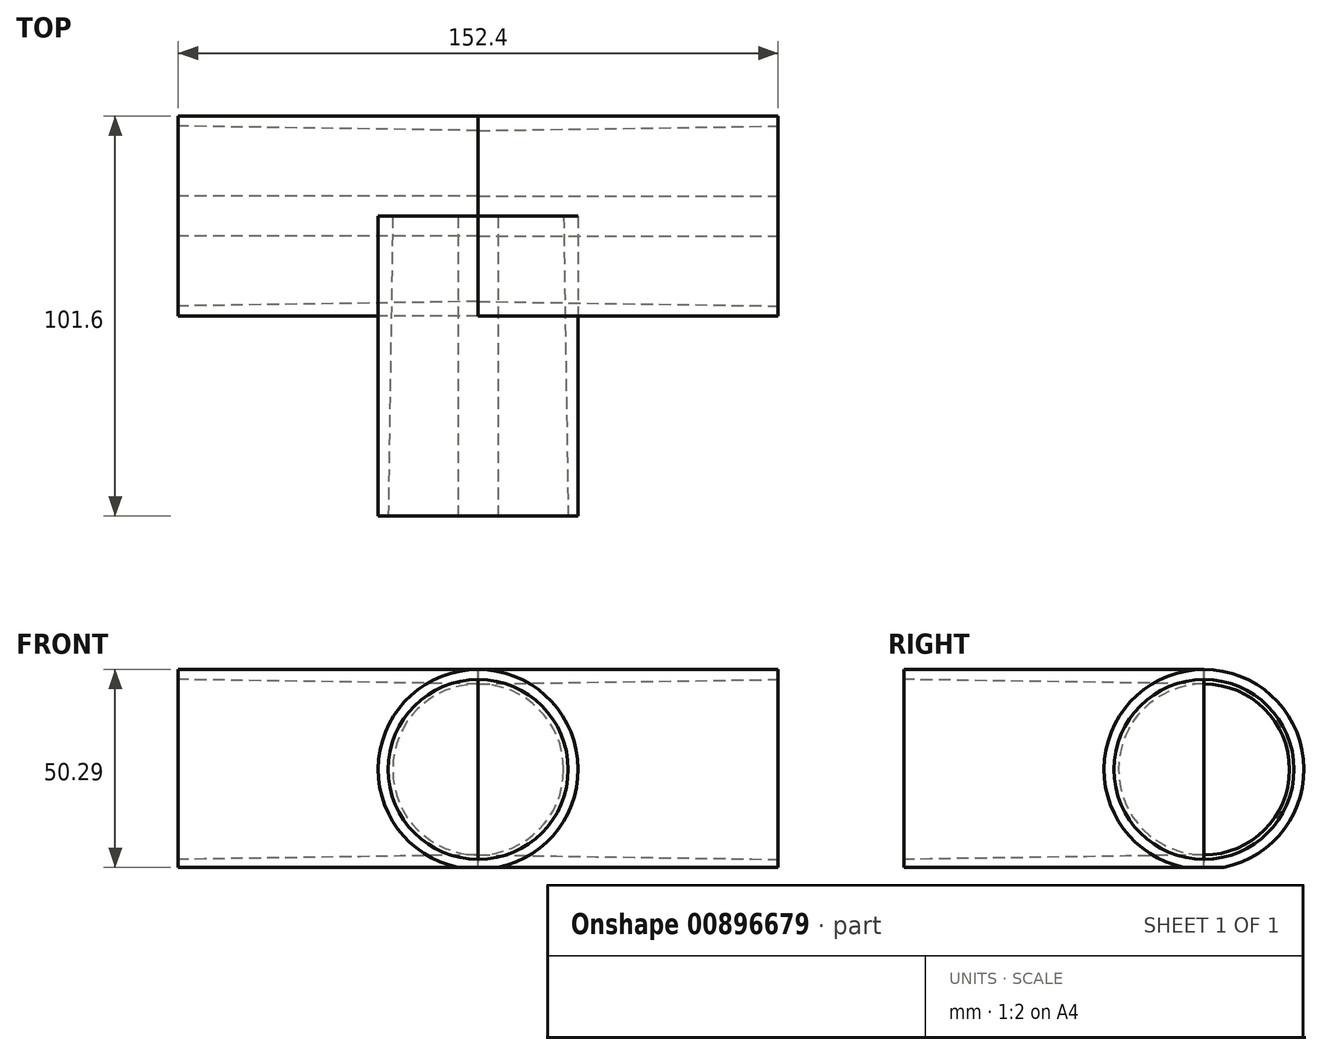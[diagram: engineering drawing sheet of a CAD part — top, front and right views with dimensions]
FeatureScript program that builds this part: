
annotation { "Feature Type Name" : "Feature", "Feature Type Description" : "" }
export const myFeature = defineFeature(function(context is Context, id is Id, definition is map)
    precondition{}
    {
        {
            var Q0;
            Q0=qCreatedBy(makeId("Front.planeOp"),FACE);
            var sketch = newSketch(context, id + "F0", { "sketchPlane" : qUnion([Q0])});
            skLineSegment(sketch, "E0", {"start": v(0, 0) * mm, "end": v(-103.9, 0) * mm, "construction": true});
            skLineSegment(sketch, "E1", {"start": v(0, 25.4) * mm, "end": v(0, 21.72) * mm});
            skLineSegment(sketch, "E2", {"start": v(0, 21.72) * mm, "end": v(76.2, 22.86) * mm});
            skLineSegment(sketch, "E3", {"start": v(76.2, 22.86) * mm, "end": v(76.2, 25.4) * mm});
            skLineSegment(sketch, "E4", {"start": v(76.2, 25.4) * mm, "end": v(0, 25.4) * mm});
            skPoint(sketch, "E5", {"position": v(50.8, 22.48) * mm});
            skSolve(sketch);
        }
        {
            var Q0;
            Q0=qSketchRegion(id+"F0",true);
            var Q1;
            Q1=sQuery(id+"F0.wireOp",EDGE,"E0");
            revolve(context, id + "F1", {"surfaceOperationType" : NewSurfaceOperationType.NEW, "entities" : qUnion([Q0]), "axis" : qUnion([Q1]), "revolveType" : RevolveType.FULL});
        }
        {
            var Q0;
            Q0=qCreatedBy(makeId("Right.planeOp"),FACE);
            cPlane(context, id + "F2", {"entities" : qUnion([Q0]), "cplaneType" : CPlaneType.OFFSET, "offset" : 0 * mm, "oppositeDirection" : true, "width" : 152.4 * mm, "height" : 152.4 * mm});
        }
        {
            var Q0;
            Q0=qCreatedBy(id+"F2.planeOp",FACE);
            var sketch = newSketch(context, id + "F3", { "sketchPlane" : qUnion([Q0])});
            skLineSegment(sketch, "E6", {"start": v(0, 0) * mm, "end": v(0, 10.77) * mm, "construction": true});
            skSolve(sketch);
        }
        {
            var Q0;
            Q0=makeQuery(id+"F1.opRevolve","SWEPT_BODY",BODY,{"disambiguationData":[OSD([sQuery(id+"F0.wireOp",EDGE,"E1"),sQuery(id+"F0.wireOp",EDGE,"E2"),sQuery(id+"F0.wireOp",EDGE,"E3"),sQuery(id+"F0.wireOp",EDGE,"E4")])]});
            var Q1;
            Q1=sQuery(id+"F3.wireOp",EDGE,"E6");
            circularPattern(context, id + "F4", {"entities" : qUnion([Q0]), "axis" : qUnion([Q1]), "angle" : 180 * degree, "instanceCount" : 3, "oppositeDirection" : true, "equalSpace" : true});
        }
        {
            var Q0;
            Q0=qCreatedBy(makeId("Right.planeOp"),FACE);
            var sketch = newSketch(context, id + "F5", { "sketchPlane" : qUnion([Q0])});
            skLineSegment(sketch, "E7.bottom", {"start": v(-127, -24.9) * mm, "end": v(25.4, -24.9) * mm});
            skLineSegment(sketch, "E7.top", {"start": v(-127, -25.4) * mm, "end": v(25.4, -25.4) * mm});
            skLineSegment(sketch, "E7.left", {"start": v(-127, -25.4) * mm, "end": v(-127, -24.9) * mm});
            skLineSegment(sketch, "E7.right", {"start": v(25.4, -25.4) * mm, "end": v(25.4, -24.9) * mm});
            skSolve(sketch);
        }
        {
            var Q0;
            Q0=qSketchRegion(id+"F5",true);
            extrude(context, id + "F6", {"entities" : qUnion([Q0]), "operationType" : NewBodyOperationType.REMOVE, "endBound" : BoundingType.THROUGH_ALL, "oppositeDirection" : true, "depth" : 25.4 * mm, "offsetDistance" : 25.4 * mm, "hasSecondDirection" : true, "secondDirectionBound" : SecondDirectionBoundingType.THROUGH_ALL, "secondDirectionOppositeDirection" : false, "secondDirectionDepth" : 25.4 * mm});
        }
    });
